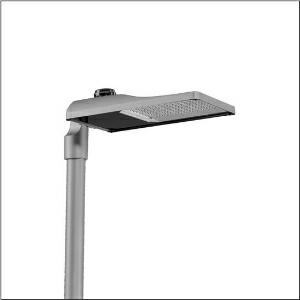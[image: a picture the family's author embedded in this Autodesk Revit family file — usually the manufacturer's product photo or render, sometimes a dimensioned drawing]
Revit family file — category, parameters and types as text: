
# Revit family: streetlight_sl_31_maxi___pl52_5xh8h75n08sa_385d
name_source: partatom
category: Lighting Fixtures
units: mm (PartAtom-declared; Revit-internal decimal feet)

## family parameters
Cut with Voids When Loaded = No
Host = Face
Light Source = No
Part Type = Normal
Room Calculation Point = No
Round Connector Dimension = Use Diameter
Shared = No

## types (1)
- --- (1 x LED, 22010 lm, 208.6 W, 2200K)
    Apparent Load = 209 VA
    CIE Flux Codes = 27 59 98 100 100
    Color Rendering = 70
    Color Temperature = 2200K
    Default Elevation = 1800 mm
    Description = Streetlight SL 31 maxi NEMA (7pin), Desk-Remote mast luminaire for post-top, side-entry; light control with lens of PMMA; light distribution: PL52, direct asymmetric distribution, for standard-compliant lighting for roads and squares; LED: luminous flux: 22.010lm, light colour: 722, colour temperature: 2200K; luminous efficacy: 105,5lm/W; control: pre-setting: linear dimming characteristic, flexible luminous flux parameterisation, time-dependent luminous flux control, constant luminous flux control, intelligent temperature release in ECG and LED module, overheat protection; luminaire housing, of diecast aluminium, SITECO metallic grey (DB 702S), corrosivity category C5 high according to DIN EN ISO 12944; cover of toughened safety glass, transparent, opened without tools; mast flange of diecast aluminium, SITECO metallic grey (DB 702S), spigot size: 76/60mm, mast flange included unmounted; with cable H07RN-F 3x 1.5mm², cable length: 14,5m, connection cable pre-assembled; mains connection: 220..240V, AC, 50/60Hz; power consumption (at start of service life): 208,6W / (at end of service life): 233,1W / (with reduced operation 50%): 88W; protection rating (complete): IP66; insulation class (complete): insulation class I (protective earthing); impact resistance: IK10; certification: CE, ENEC, ENEC+, VDE, UKCA; permissible operating ambient temperature for outdoor applications: -40..+50°C; packaging unit: 1 piece

Light Distribution: PL52
    Height = 79 mm
    Lamp = 1 x LED
    Lamp Light Flux = 22010 lm
    Lamp Power = 208.6 W
    Lamp count = 1
    Length = 657 mm
    Luminous efficacy = 106 lm/W
    Manufacturer = Siteco
    ModVariant = No
    Model = 5XH8H75N08SA
    Number of Poles = 1
    OnlyDefault = Yes
    Power Factor = 1
    Product Name = Streetlight SL 31 maxi | PL52
    Product group = mast luminaire | pylon top
    ProductGroupID = 6100
    Protection Class = Protection class I
    Protection Degree = IP 66
    RLX_Detail_Level = 1
    RLX_Emergency_Light_Flux = 0 lm
    RLX_Emergency_Type = 0
    RLX_Emergency_Type_DB = No
    RlxData = <blob elided: 36593 chars, md5=42b6c1e9>
    Socket = socket
    Standby Power = 0 W
    System Light Flux = 22009 lm
    System Power = 209 W
    Type Comments = factory setting: luminous flux: 100 % | dim-lin: 254 | 718 mA
    Type Image = l_1300293.jpg
    URL = http://relux.com
    VarID = @adj_008869
    Voltage = 0 V
    Weight = 0.00 kg
    Width = 362 mm

## geometry (parser evidence)
native form markers: Blend x4, Sweep x10
no freeform markers — native parametric forms only
